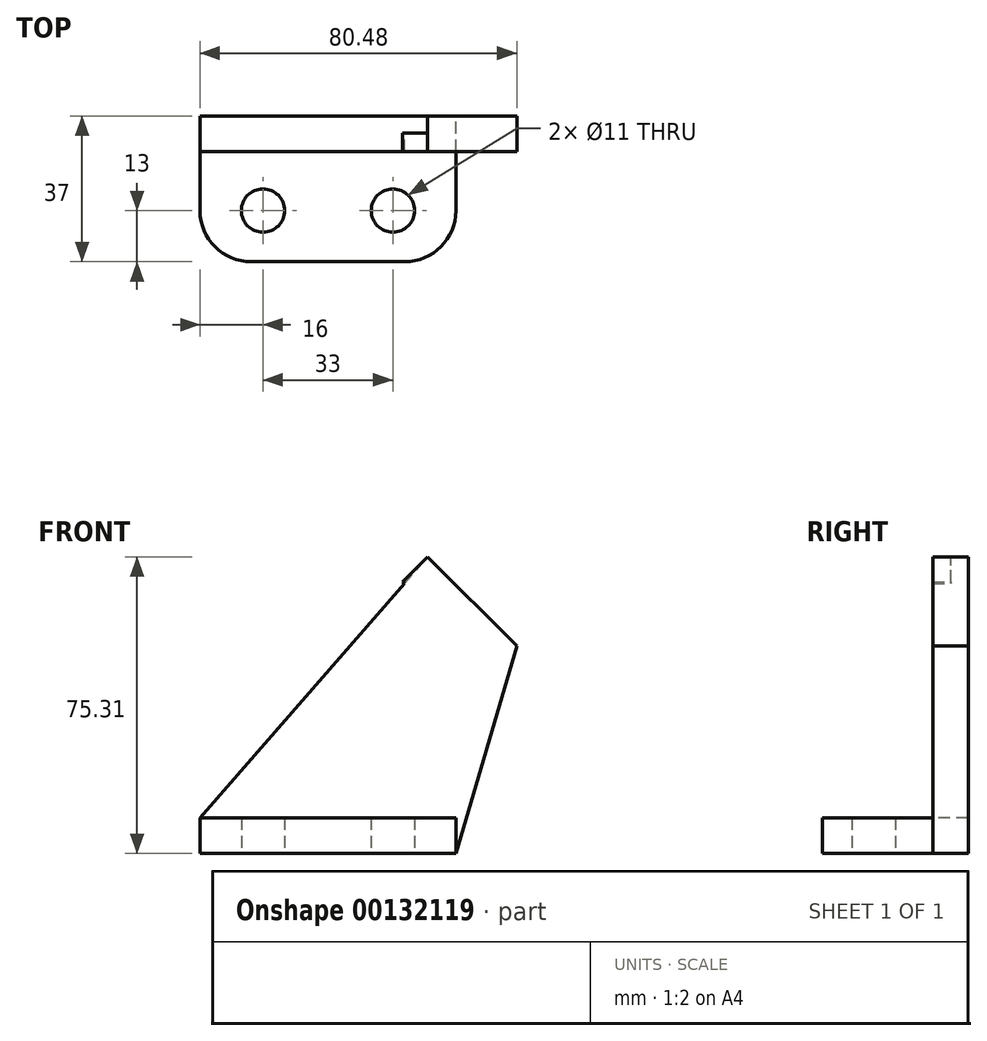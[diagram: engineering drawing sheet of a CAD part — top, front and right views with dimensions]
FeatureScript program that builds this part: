
annotation { "Feature Type Name" : "Feature", "Feature Type Description" : "" }
export const myFeature = defineFeature(function(context is Context, id is Id, definition is map)
    precondition{}
    {
        {
            var Q0;
            Q0=qCreatedBy(makeId("Top.planeOp"),FACE);
            var sketch = newSketch(context, id + "F0", { "sketchPlane" : qUnion([Q0])});
            skCircle(sketch, "E0", {"center": v(16, 0) * mm, "radius": 5.5 * mm});
            skCircle(sketch, "E1", {"center": v(49, 0) * mm, "radius": 5.5 * mm});
            skLineSegment(sketch, "E2", {"start": v(0, 24) * mm, "end": v(0, 0) * mm});
            skLineSegment(sketch, "E3", {"start": v(13, -13) * mm, "end": v(52, -13) * mm});
            skLineSegment(sketch, "E4", {"start": v(65, 0) * mm, "end": v(65, 24) * mm});
            skPoint(sketch, "E5.visualSharp", {"position": v(0, -13) * mm});
            skArc(sketch, "E5.filletArc", {"start": v(0, 0) * mm, "mid": v(3.8, -9.2) * mm, "end": v(13, -13) * mm});
            skPoint(sketch, "E6.visualSharp", {"position": v(65, -13) * mm});
            skArc(sketch, "E6.filletArc", {"start": v(52, -13) * mm, "mid": v(61.2, -9.2) * mm, "end": v(65, 0) * mm});
            skLineSegment(sketch, "E7", {"start": v(0, 24) * mm, "end": v(65, 24) * mm});
            skSolve(sketch);
        }
        {
            var Q0;
            Q0 = qSketchRegion(id + "F0", true);
            extrude(context, id + "F1", {"entities" : qUnion([Q0]), "depth" : 9 * mm});
        }
        {
            var Q0;
            Q0=makeQuery(id+"F1.opExtrude","SWEPT_FACE",FACE,{"disambiguationData":[OSD([sQuery(id+"F0.wireOp",EDGE,"E7")])]});
            var sketch = newSketch(context, id + "F2", { "sketchPlane" : qUnion([Q0])});
            skLineSegment(sketch, "E8", {"start": v(0, 9) * mm, "end": v(-57.85, 75.31) * mm});
            skLineSegment(sketch, "E9", {"start": v(-65, 0) * mm, "end": v(-80.48, 52.69) * mm});
            skLineSegment(sketch, "E10", {"start": v(-80.48, 52.69) * mm, "end": v(-57.85, 75.31) * mm});
            skLineSegment(sketch, "E11", {"start": v(-69.16, 64) * mm, "end": v(-79.4, 74.24) * mm, "construction": true});
            skLineSegment(sketch, "E12", {"start": v(-69.16, 64) * mm, "end": v(-85.68, 64) * mm, "construction": true});
            skLineSegment(sketch, "E13", {"start": v(-85.68, 64) * mm, "end": v(-63.85, 64) * mm, "construction": true});
            skSolve(sketch);
        }
        {
            var Q0;
            Q0=makeQuery(id+"F2.imprint","IMPRINT",FACE,{"disambiguationData":[TD([[makeQuery(id+"F2.imprint","IMPRINT",EDGE,{"derivedFrom":sQuery(id+"F2.wireOp",EDGE,"E8")}),1.0]])]});
            extrude(context, id + "F3", {"entities" : qUnion([Q0]), "operationType" : NewBodyOperationType.ADD, "oppositeDirection" : true, "depth" : 9 * mm});
        }
        {
            var Q0;
            Q0=makeQuery(id+"F3.opExtrude","SWEPT_FACE",FACE,{"disambiguationData":[OSD([sQuery(id+"F2.wireOp",EDGE,"E10")])]});
            var sketch = newSketch(context, id + "F4", { "sketchPlane" : qUnion([Q0])});
            skLineSegment(sketch, "E14", {"start": v(-12.35, 24) * mm, "end": v(-12.35, -5) * mm});
            skLineSegment(sketch, "E15", {"start": v(19.65, 24) * mm, "end": v(19.65, -5) * mm});
            skArc(sketch, "E16", {"start": v(-12.35, -5) * mm, "mid": v(3.65, -21) * mm, "end": v(19.65, -5) * mm});
            skCircle(sketch, "E17", {"center": v(3.65, -5) * mm, "radius": 7 * mm});
            skSolve(sketch);
        }
        {
            var Q0;
            {var subQ0=sQuery(id+"F4.wireOp",EDGE,"E16");Q0=makeQuery(id+"F4.imprint","IMPRINT",FACE,{"disambiguationData":[TD([[makeQuery(id+"F4.imprint","IMPRINT",EDGE,{"derivedFrom":subQ0}),1.0]])]});}
            extrude(context, id + "F5", {"entities" : qUnion([Q0]), "operationType" : NewBodyOperationType.ADD, "oppositeDirection" : true, "depth" : 9 * mm});
        }
    });
